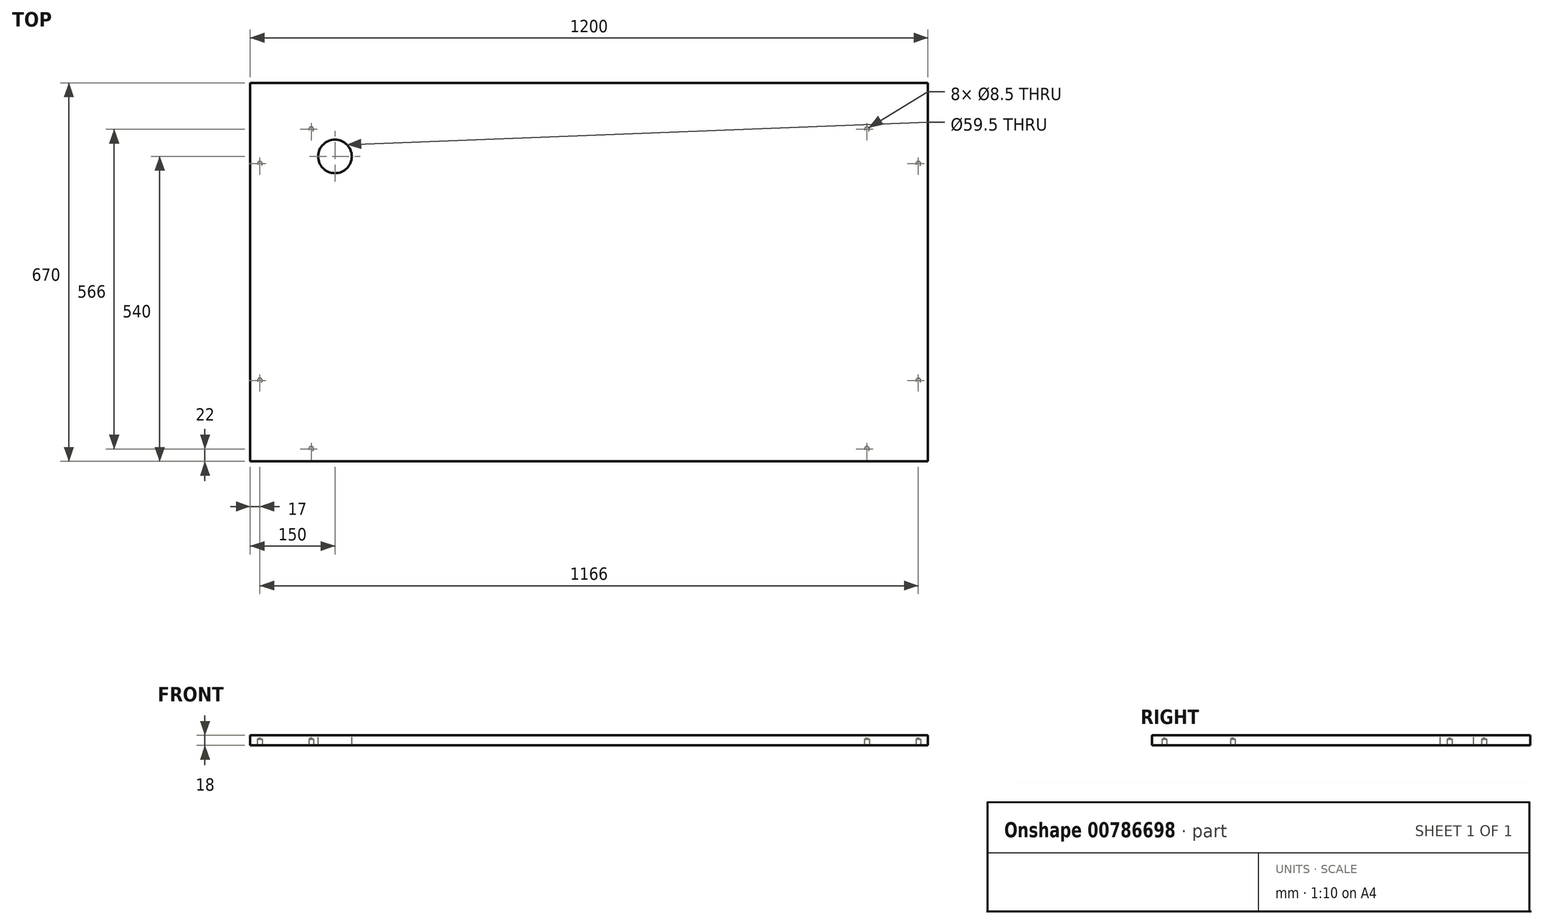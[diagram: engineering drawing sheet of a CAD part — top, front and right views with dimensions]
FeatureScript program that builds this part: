
annotation { "Feature Type Name" : "Feature", "Feature Type Description" : "" }
export const myFeature = defineFeature(function(context is Context, id is Id, definition is map)
    precondition{}
    {
        {
            var Q0;
            Q0=qCreatedBy(makeId("Top.planeOp"),FACE);
            var sketch = newSketch(context, id + "F0", { "sketchPlane" : qUnion([Q0])});
            skLineSegment(sketch, "E0.bottom", {"start": v(600, -335) * mm, "end": v(-600, -335) * mm});
            skLineSegment(sketch, "E0.top", {"start": v(600, 335) * mm, "end": v(-600, 335) * mm});
            skLineSegment(sketch, "E0.left", {"start": v(600, -335) * mm, "end": v(600, 335) * mm});
            skLineSegment(sketch, "E0.right", {"start": v(-600, -335) * mm, "end": v(-600, 335) * mm});
            skPoint(sketch, "E0.middle", {"position": v(0, 0) * mm});
            skSolve(sketch);
        }
        {
            var Q0;
            Q0 = qSketchRegion(id + "F0", true);
            extrude(context, id + "F1", {"entities" : qUnion([Q0]), "depth" : 18 * mm, "offsetDistance" : 25 * mm});
        }
        {
            var Q0;
            Q0=makeQuery(id+"F1.opExtrude","CAP_FACE",FACE,{"disambiguationData":[OSD([sQuery(id+"F0.wireOp",EDGE,"E0.bottom"),sQuery(id+"F0.wireOp",EDGE,"E0.top"),sQuery(id+"F0.wireOp",EDGE,"E0.left"),sQuery(id+"F0.wireOp",EDGE,"E0.right")])],"isStart":false});
            var sketch = newSketch(context, id + "F2", { "sketchPlane" : qUnion([Q0])});
            skPoint(sketch, "E1", {"position": v(-450, 205) * mm});
            skSolve(sketch);
        }
        {
            var Q0;
            Q0=sQuery(id+"F2.wireOp",VERTEX,"E1");
            var Q1;
            Q1=makeQuery(id+"F1.opExtrude","SWEPT_BODY",BODY,{"disambiguationData":[OSD([sQuery(id+"F0.wireOp",EDGE,"E0.bottom"),sQuery(id+"F0.wireOp",EDGE,"E0.top"),sQuery(id+"F0.wireOp",EDGE,"E0.left"),sQuery(id+"F0.wireOp",EDGE,"E0.right")])]});
            hole(context, id + "F3", {"style" : HoleStyle.SIMPLE, "endStyle" : HoleEndStyle.THROUGH, "holeDiameter" : 59.5 * mm, "majorDiameter" : 5 * mm, "isTappedThrough" : true, "tappedDepth" : 6.5 * mm, "tapClearance" : 3, "locations" : qUnion([Q0]), "scope" : qUnion([Q1])});
        }
        {
            var Q0;
            Q0=makeQuery(id+"F1.opExtrude","CAP_FACE",FACE,{"disambiguationData":[OSD([sQuery(id+"F0.wireOp",EDGE,"E0.bottom"),sQuery(id+"F0.wireOp",EDGE,"E0.top"),sQuery(id+"F0.wireOp",EDGE,"E0.left"),sQuery(id+"F0.wireOp",EDGE,"E0.right")])],"isStart":true});
            var sketch = newSketch(context, id + "F4", { "sketchPlane" : qUnion([Q0])});
            skLineSegment(sketch, "E2.bottom", {"start": v(492, -253) * mm, "end": v(-492, -253) * mm, "construction": true});
            skLineSegment(sketch, "E2.top", {"start": v(492, 313) * mm, "end": v(-492, 313) * mm, "construction": true});
            skLineSegment(sketch, "E2.left", {"start": v(492, -253) * mm, "end": v(492, 313) * mm, "construction": true});
            skLineSegment(sketch, "E2.right", {"start": v(-492, -253) * mm, "end": v(-492, 313) * mm, "construction": true});
            skLineSegment(sketch, "E3", {"start": v(0, -335) * mm, "end": v(0, 335) * mm, "construction": true});
            skLineSegment(sketch, "E4.bottom", {"start": v(-583, 192) * mm, "end": v(583, 192) * mm, "construction": true});
            skLineSegment(sketch, "E4.top", {"start": v(-583, -192) * mm, "end": v(583, -192) * mm, "construction": true});
            skLineSegment(sketch, "E4.left", {"start": v(-583, 192) * mm, "end": v(-583, -192) * mm, "construction": true});
            skLineSegment(sketch, "E4.right", {"start": v(583, 192) * mm, "end": v(583, -192) * mm, "construction": true});
            skPoint(sketch, "E4.middle", {"position": v(0, 0) * mm});
            skSolve(sketch);
        }
        {
            var Q0;
            Q0=sQuery(id+"F4.wireOp",VERTEX,"E2.bottom.end");
            var Q1;
            Q1=sQuery(id+"F4.wireOp",VERTEX,"E4.top.start");
            var Q2;
            Q2=sQuery(id+"F4.wireOp",VERTEX,"E4.bottom.start");
            var Q3;
            Q3=sQuery(id+"F4.wireOp",VERTEX,"E4.bottom.end");
            var Q4;
            Q4=sQuery(id+"F4.wireOp",VERTEX,"E2.top.start");
            var Q5;
            Q5=sQuery(id+"F4.wireOp",VERTEX,"E4.top.end");
            var Q6;
            Q6=sQuery(id+"F4.wireOp",VERTEX,"E2.bottom.start");
            var Q7;
            Q7=sQuery(id+"F4.wireOp",VERTEX,"E2.top.end");
            var Q8;
            Q8=makeQuery(id+"F1.opExtrude","SWEPT_BODY",BODY,{"disambiguationData":[OSD([sQuery(id+"F0.wireOp",EDGE,"E0.bottom"),sQuery(id+"F0.wireOp",EDGE,"E0.top"),sQuery(id+"F0.wireOp",EDGE,"E0.left"),sQuery(id+"F0.wireOp",EDGE,"E0.right")])]});
            hole(context, id + "F5", {"style" : HoleStyle.SIMPLE, "endStyle" : HoleEndStyle.BLIND, "standardTappedOrClearance" : lookupTablePath({ "standard" : "ISO", "engagement" : "75%", "pitch" : "1.5 mm", "size" : "M10", "type" : "Tapped" }), "standardBlindInLast" : lookupTablePath({ "standard" : "ISO", "engagement" : "75%", "pitch" : "1.5 mm", "size" : "M10", "type" : "Tapped" }), "holeDiameter" : 8.5 * mm, "majorDiameter" : 10 * mm, "showTappedDepth" : true, "holeDepth" : 11 * mm, "isTappedThrough" : true, "tappedDepth" : 6.5 * mm, "tapClearance" : 3, "locations" : qUnion([Q0, Q1, Q2, Q3, Q4, Q5, Q6, Q7]), "scope" : qUnion([Q8])});
        }
    });
